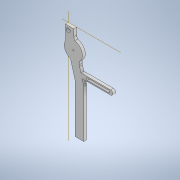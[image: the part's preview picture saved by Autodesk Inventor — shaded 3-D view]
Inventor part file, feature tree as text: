
AUTODESK INVENTOR PART (.ipt)
format: ipt  version: 2022 (Build 260153000, 153)  size: 140,288 bytes
history: native  units: mm
features: other x1, extrude x1, sketch x1
ambient origin geometry x8: Origin, YZ Plane, XZ Plane, XY Plane, X Axis, Y Axis, Z Axis, Center Point
bodies: Body1 (feature_tree)
feature tree (3):
  other  "Sólido1"
  extrude  "Extrusión1"  Depth=5.0mm TaperAngle=0.0deg
  sketch  "Boceto1"  dims[d0=2.0mm d1=5.0mm d2=0.0mm]
